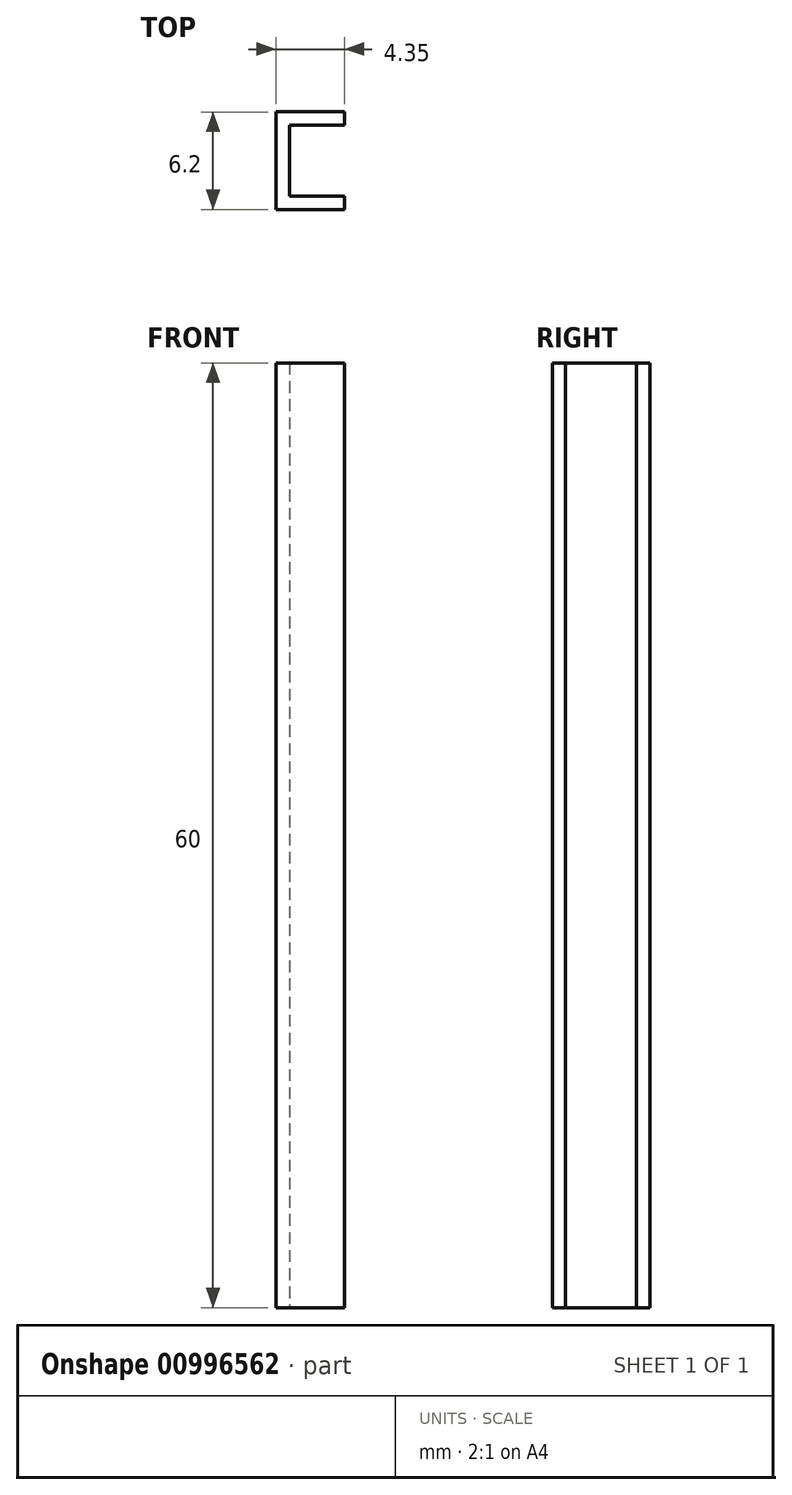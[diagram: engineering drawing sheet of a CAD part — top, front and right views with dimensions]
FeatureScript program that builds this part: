
annotation { "Feature Type Name" : "Feature", "Feature Type Description" : "" }
export const myFeature = defineFeature(function(context is Context, id is Id, definition is map)
    precondition{}
    {
        {
            var Q0;
            Q0=qCreatedBy(makeId("Top.planeOp"),FACE);
            var sketch = newSketch(context, id + "F0", { "sketchPlane" : qUnion([Q0])});
            skLineSegment(sketch, "E0", {"start": v(-18.38, 12.6) * mm, "end": v(-18.38, 6.4) * mm});
            skLineSegment(sketch, "E1", {"start": v(-18.38, 6.4) * mm, "end": v(-14.03, 6.4) * mm});
            skLineSegment(sketch, "E2", {"start": v(-14.03, 6.4) * mm, "end": v(-14.03, 7.25) * mm});
            skLineSegment(sketch, "E3", {"start": v(-14.03, 7.25) * mm, "end": v(-17.53, 7.25) * mm});
            skLineSegment(sketch, "E4", {"start": v(-17.53, 7.25) * mm, "end": v(-17.53, 11.75) * mm});
            skLineSegment(sketch, "E5", {"start": v(-17.53, 11.75) * mm, "end": v(-14.03, 11.75) * mm});
            skLineSegment(sketch, "E6", {"start": v(-14.03, 11.75) * mm, "end": v(-14.03, 12.6) * mm});
            skLineSegment(sketch, "E7", {"start": v(-14.03, 12.6) * mm, "end": v(-18.38, 12.6) * mm});
            skSolve(sketch);
        }
        {
            var Q0;
            Q0 = qSketchRegion(id + "F0", true);
            extrude(context, id + "F1", {"entities" : qUnion([Q0]), "depth" : 60 * mm, "offsetDistance" : 25 * mm});
        }
    });
